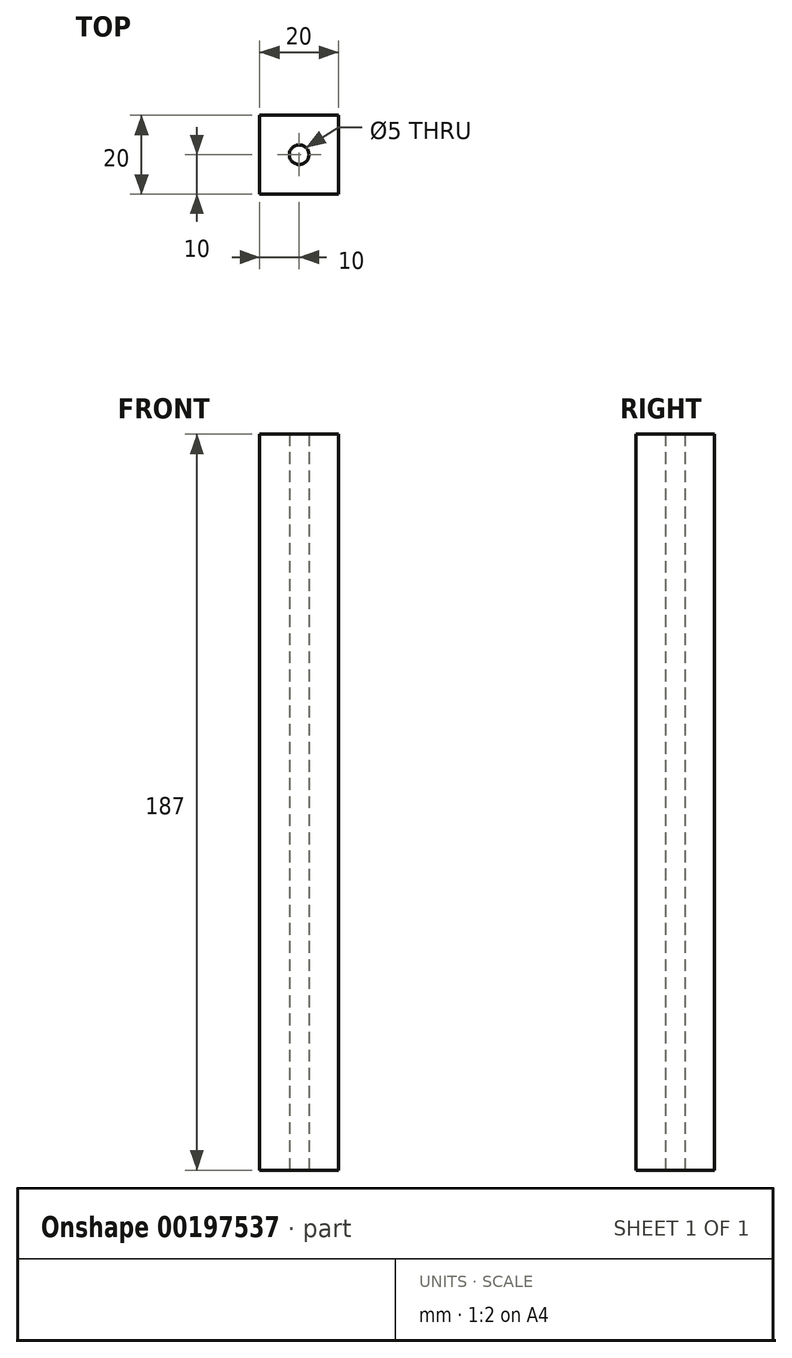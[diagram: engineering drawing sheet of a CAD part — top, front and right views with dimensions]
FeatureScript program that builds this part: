
annotation { "Feature Type Name" : "Feature", "Feature Type Description" : "" }
export const myFeature = defineFeature(function(context is Context, id is Id, definition is map)
    precondition{}
    {
        {
            var Q0;
            Q0=qCreatedBy(makeId("Top.planeOp"),FACE);
            var sketch = newSketch(context, id + "F0", { "sketchPlane" : qUnion([Q0])});
            skLineSegment(sketch, "E0.bottom", {"start": v(-10, 10) * mm, "end": v(10, 10) * mm});
            skLineSegment(sketch, "E0.top", {"start": v(-10, -10) * mm, "end": v(10, -10) * mm});
            skLineSegment(sketch, "E0.left", {"start": v(-10, 10) * mm, "end": v(-10, -10) * mm});
            skLineSegment(sketch, "E0.right", {"start": v(10, 10) * mm, "end": v(10, -10) * mm});
            skCircle(sketch, "E1", {"center": v(0, 0) * mm, "radius": 2.5 * mm});
            skSolve(sketch);
        }
        {
            var Q0;
            Q0=qSketchRegion(id+"F0",true);
            extrude(context, id + "F1", {"entities" : qUnion([Q0]), "depth" : 187 * mm});
        }
        {
            var Q0;
            Q0=makeQuery(id+"F1.opExtrude","SWEPT_FACE",FACE,{"disambiguationData":[OSD([sQuery(id+"F0.wireOp",EDGE,"E0.right")])]});
            var sketch = newSketch(context, id + "F2", { "sketchPlane" : qUnion([Q0])});
            skCircle(sketch, "E2", {"center": v(0, 10) * mm, "radius": 2.5 * mm});
            skSolve(sketch);
        }
    });
